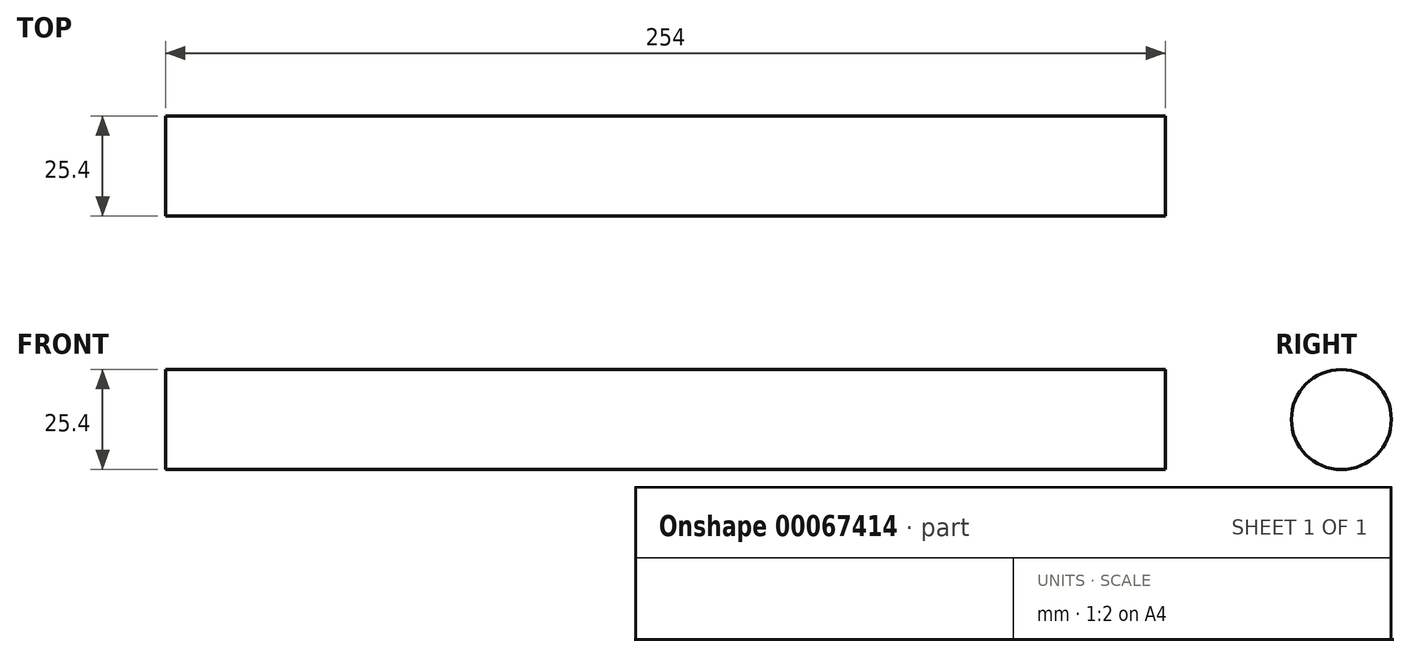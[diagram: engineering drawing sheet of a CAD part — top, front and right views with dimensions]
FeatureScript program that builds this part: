
annotation { "Feature Type Name" : "Feature", "Feature Type Description" : "" }
export const myFeature = defineFeature(function(context is Context, id is Id, definition is map)
    precondition{}
    {
        {
            var Q0;
            Q0=qCreatedBy(makeId("Right.planeOp"),FACE);
            var sketch = newSketch(context, id + "F0", { "sketchPlane" : qUnion([Q0])});
            skCircle(sketch, "E0", {"center": v(0, 0) * mm, "radius": 12.7 * mm});
            skSolve(sketch);
        }
        {
            var Q0;
            Q0=makeQuery(id+"F0.imprint","IMPRINT",FACE,{"disambiguationData":[TD([[makeQuery(id+"F0.imprint","IMPRINT",EDGE,{"derivedFrom":sQuery(id+"F0.wireOp",EDGE,"E0")}),1.0]])]});
            extrude(context, id + "F1", {"entities" : qUnion([Q0]), "oppositeDirection" : true, "depth" : 254 * mm});
        }
    });
